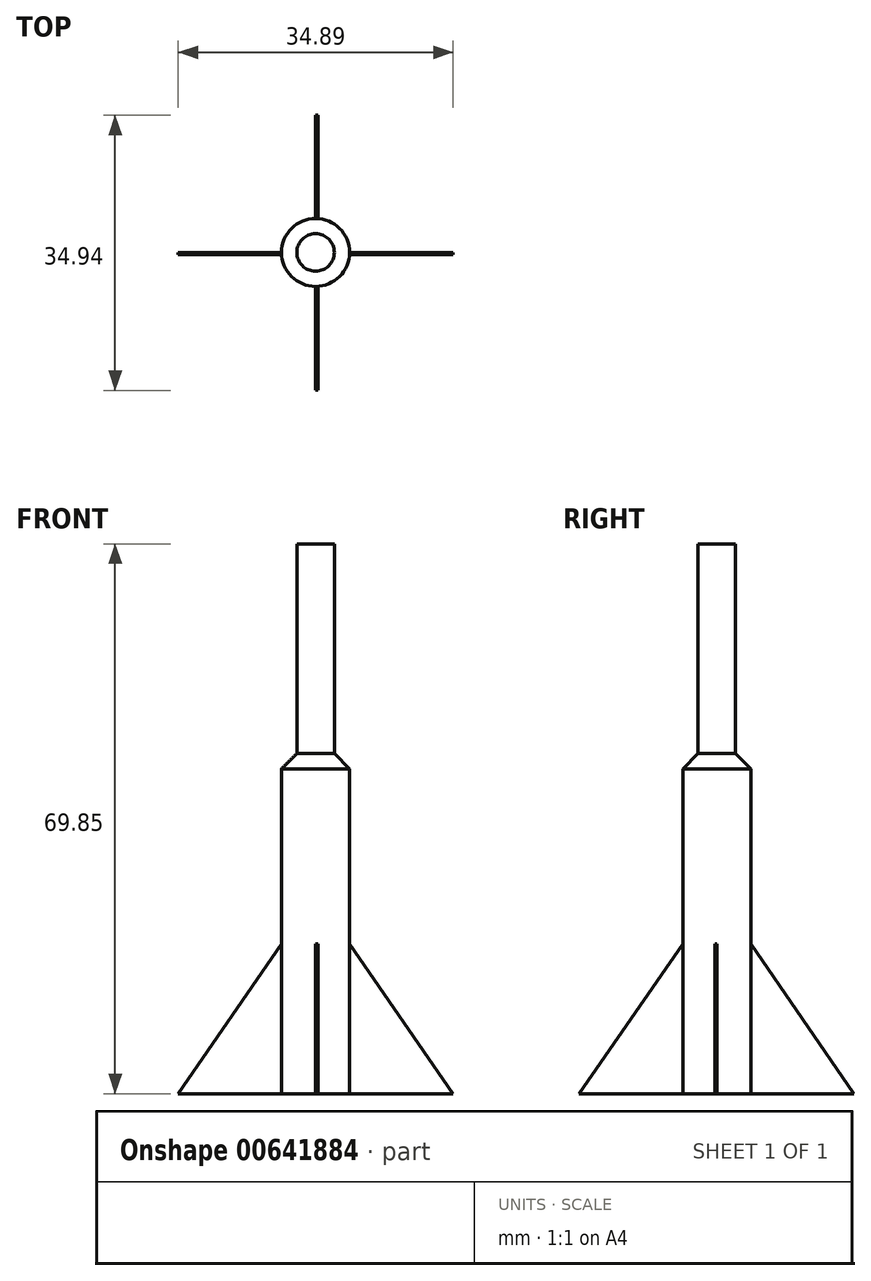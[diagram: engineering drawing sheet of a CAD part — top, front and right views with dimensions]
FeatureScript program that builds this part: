
annotation { "Feature Type Name" : "Feature", "Feature Type Description" : "" }
export const myFeature = defineFeature(function(context is Context, id is Id, definition is map)
    precondition{}
    {
        {
            var Q0;
            Q0=qCreatedBy(makeId("Top.planeOp"),FACE);
            var sketch = newSketch(context, id + "F0", { "sketchPlane" : qUnion([Q0])});
            skCircle(sketch, "E0", {"center": v(0, 0) * mm, "radius": 4.32 * mm});
            skSolve(sketch);
        }
        {
            var Q0;
            Q0 = qSketchRegion(id + "F0", true);
            extrude(context, id + "F1", {"entities" : qUnion([Q0]), "depth" : 44.45 * mm, "offsetDistance" : 25.4 * mm});
        }
        {
            var Q0;
            Q0=makeQuery(id+"F1.opExtrude","CAP_FACE",FACE,{"disambiguationData":[OSD([sQuery(id+"F0.wireOp",EDGE,"E0")])],"isStart":false});
            var sketch = newSketch(context, id + "F2", { "sketchPlane" : qUnion([Q0])});
            skCircle(sketch, "E1", {"center": v(0, 0) * mm, "radius": 2.38 * mm});
            skSolve(sketch);
        }
        {
            var Q0;
            Q0 = qSketchRegion(id + "F2", true);
            extrude(context, id + "F3", {"entities" : qUnion([Q0]), "operationType" : NewBodyOperationType.ADD, "depth" : 25.4 * mm, "offsetDistance" : 25.4 * mm});
        }
        {
            var Q0;
            Q0=makeQuery(id+"F1.opExtrude","CAP_EDGE",EDGE,{"disambiguationData":[OSD([sQuery(id+"F0.wireOp",EDGE,"E0")])],"isStart":false});
            chamfer(context, id + "F4", {"entities" : qUnion([Q0]), "width" : 3.17 * mm, "tangentPropagation" : true});
        }
        {
            var Q0;
            Q0=makeQuery(id+"F1.opExtrude","CAP_FACE",FACE,{"disambiguationData":[OSD([sQuery(id+"F0.wireOp",EDGE,"E0")])],"isStart":true});
            var sketch = newSketch(context, id + "F5", { "sketchPlane" : qUnion([Q0])});
            skLineSegment(sketch, "E2", {"start": v(-4.32, 0) * mm, "end": v(4.32, 0) * mm});
            skLineSegment(sketch, "E3", {"start": v(0, 4.32) * mm, "end": v(0, -4.32) * mm});
            skLineSegment(sketch, "E4", {"start": v(4.32, 0) * mm, "end": v(17.45, 0) * mm});
            skLineSegment(sketch, "E5", {"start": v(-4.32, 0) * mm, "end": v(-17.45, 0) * mm});
            skLineSegment(sketch, "E6", {"start": v(0, -4.32) * mm, "end": v(0, -17.43) * mm});
            skLineSegment(sketch, "E7", {"start": v(0, 4.32) * mm, "end": v(0, 17.52) * mm});
            skLineSegment(sketch, "E8.bottom", {"start": v(0, 4.32) * mm, "end": v(0.34, 4.32) * mm});
            skLineSegment(sketch, "E8.top", {"start": v(0, 17.52) * mm, "end": v(0.34, 17.52) * mm});
            skLineSegment(sketch, "E8.right", {"start": v(0.34, 4.32) * mm, "end": v(0.34, 17.52) * mm});
            skLineSegment(sketch, "E9.bottom", {"start": v(0, -4.32) * mm, "end": v(0.34, -4.32) * mm});
            skLineSegment(sketch, "E9.top", {"start": v(0, -17.42) * mm, "end": v(0.34, -17.42) * mm});
            skLineSegment(sketch, "E9.left", {"start": v(0, -4.32) * mm, "end": v(0, -17.42) * mm});
            skLineSegment(sketch, "E9.right", {"start": v(0.34, -4.32) * mm, "end": v(0.34, -17.42) * mm});
            skLineSegment(sketch, "E10.top", {"start": v(4.32, 0.26) * mm, "end": v(17.45, 0.26) * mm});
            skLineSegment(sketch, "E10.left", {"start": v(4.32, 0) * mm, "end": v(4.32, 0.26) * mm});
            skLineSegment(sketch, "E10.right", {"start": v(17.45, 0) * mm, "end": v(17.45, 0.26) * mm});
            skLineSegment(sketch, "E11.bottom", {"start": v(-4.32, 0) * mm, "end": v(-17.44, 0) * mm});
            skLineSegment(sketch, "E11.top", {"start": v(-4.32, 0.26) * mm, "end": v(-17.44, 0.26) * mm});
            skLineSegment(sketch, "E11.left", {"start": v(-4.32, 0) * mm, "end": v(-4.32, 0.26) * mm});
            skLineSegment(sketch, "E11.right", {"start": v(-17.44, 0) * mm, "end": v(-17.44, 0.26) * mm});
            skSolve(sketch);
        }
        {
            var Q0;
            Q0 = qSketchRegion(id + "F5", true);
            extrude(context, id + "F6", {"entities" : qUnion([Q0]), "depth" : -19.05 * mm, "offsetDistance" : 25.4 * mm});
        }
        {
            var Q0;
            Q0=makeQuery(id+"F6.opExtrude","SWEPT_FACE",FACE,{"disambiguationData":[OSD([sQuery(id+"F5.wireOp",EDGE,"E8.right")])]});
            var sketch = newSketch(context, id + "F7", { "sketchPlane" : qUnion([Q0])});
            skLineSegment(sketch, "E12", {"start": v(-4.32, 19.05) * mm, "end": v(-17.52, 0) * mm});
            skSolve(sketch);
        }
        {
            var Q0;
            Q0=makeQuery(id+"F7.imprint","IMPRINT",FACE,{"disambiguationData":[TD([[makeQuery(id+"F7.imprint","IMPRINT",EDGE,{"derivedFrom":sQuery(id+"F7.wireOp",EDGE,"E12")}),-1.0]])]});
            extrude(context, id + "F8", {"entities" : qUnion([Q0]), "operationType" : NewBodyOperationType.REMOVE, "oppositeDirection" : true, "depth" : 25.4 * mm, "offsetDistance" : 25.4 * mm});
        }
        {
            var Q0;
            Q0=makeQuery(id+"F6.opExtrude","SWEPT_FACE",FACE,{"disambiguationData":[OSD([sQuery(id+"F5.wireOp",EDGE,"E9.right")])]});
            var sketch = newSketch(context, id + "F9", { "sketchPlane" : qUnion([Q0])});
            skLineSegment(sketch, "E13", {"start": v(4.32, 19.05) * mm, "end": v(17.42, 0) * mm});
            skSolve(sketch);
        }
        {
            var Q0;
            Q0 = qSketchRegion(id + "F9", true);
            var Q1;
            Q1=makeQuery(id+"F9.imprint","IMPRINT",FACE,{"disambiguationData":[TD([[makeQuery(id+"F9.imprint","IMPRINT",EDGE,{"derivedFrom":sQuery(id+"F9.wireOp",EDGE,"E13")}),1.0]])]});
            extrude(context, id + "F10", {"entities" : qUnion([Q0, Q1]), "operationType" : NewBodyOperationType.REMOVE, "oppositeDirection" : true, "depth" : 25.4 * mm, "offsetDistance" : 25.4 * mm});
        }
        {
            var Q0;
            Q0=makeQuery(id+"F6.opExtrude","SWEPT_FACE",FACE,{"disambiguationData":[OSD([sQuery(id+"F5.wireOp",EDGE,"E10.top")])]});
            var sketch = newSketch(context, id + "F11", { "sketchPlane" : qUnion([Q0])});
            skLineSegment(sketch, "E14", {"start": v(4.32, 19.05) * mm, "end": v(17.45, 0) * mm});
            skSolve(sketch);
        }
        {
            var Q0;
            Q0=makeQuery(id+"F11.imprint","IMPRINT",FACE,{"disambiguationData":[TD([[makeQuery(id+"F11.imprint","IMPRINT",EDGE,{"derivedFrom":sQuery(id+"F11.wireOp",EDGE,"E14")}),1.0]])]});
            extrude(context, id + "F12", {"entities" : qUnion([Q0]), "operationType" : NewBodyOperationType.REMOVE, "oppositeDirection" : true, "depth" : 25.4 * mm, "offsetDistance" : 25.4 * mm});
        }
        {
            var Q0;
            Q0=makeQuery(id+"F6.opExtrude","SWEPT_FACE",FACE,{"disambiguationData":[OSD([sQuery(id+"F5.wireOp",EDGE,"E11.top")])]});
            var sketch = newSketch(context, id + "F13", { "sketchPlane" : qUnion([Q0])});
            skLineSegment(sketch, "E15", {"start": v(-4.32, 19.05) * mm, "end": v(-17.44, 0) * mm});
            skSolve(sketch);
        }
        {
            var Q0;
            Q0=makeQuery(id+"F13.imprint","IMPRINT",FACE,{"disambiguationData":[TD([[makeQuery(id+"F13.imprint","IMPRINT",EDGE,{"derivedFrom":sQuery(id+"F13.wireOp",EDGE,"E15")}),-1.0]])]});
            extrude(context, id + "F14", {"entities" : qUnion([Q0]), "operationType" : NewBodyOperationType.REMOVE, "oppositeDirection" : true, "depth" : 25.4 * mm, "offsetDistance" : 25.4 * mm});
        }
    });
